# Revit family: Univers-IP44-leer-Unterputz-AT-de
name_source: partatom
category: Electrical Equipment
units: mm (PartAtom-declared; Revit-internal decimal feet)

## family parameters
Cut with Voids When Loaded = No
Host = Face
Panel Configuration = Two Columns, Circuits Across
Part Type = Panelboard
Room Calculation Point = No
Round Connector Dimension = Use Diameter
Shared = No

## types (21) — shared parameters
EF000003 - Montageart = EV001247 - Aufputz/Unterputz
EF000007 - Farbe = EV000202 - weiß
EF000116 - RAL-Nummer = 9010
EF000118 - Mit Montageplatte = No
EF000339 - Art der Abdeckung = EV004216 - Tür
EF001062 - EMV-Ausführung = No
EF001088 - Anbaumöglichkeit = No
EF001134 - DIN-Schiene = No
EF001596 - Werkstoff des Gehäuses = EV000179 - Stahl
EF005474 - Schutzart (IP) = EV006418 - IP44
EF006244 - Transparenter Deckel/Tür = No
EF006306 - Mit Schloss = No
EF015776 - Erdungsklemmenblock = No
EF015777 - Neutralleiterklemmenblock = No
EF015941 - Signaldurchlassende Tür = No
HG000002 - Mit tür = Yes
HG000003 - Bereich = Univers
HG000005 - Dicke = 3 mm  [stored 0.00984252 ft]
HG000006 - Unterputz = Yes
HG000011 - Leere Reihen von unten = No
Manufacturer = Hager
Type Comments = Univers
zero-valued in all types: Default Elevation, EF000266 - Anzahl der Reihen, EF002950 - Breite in Teilungseinheiten, HG000001 - Anzahl der Spalten, HG000007 - Anzahl der leeren Spalten, HG000008 - Anzahl der leeren Reihen

## per-type parameters (varying)
| type | EF000008 - Breite | EF000040 - Höhe | EF000049 - Tiefe | EF000218 - Einbautiefe | EF000332 - Einbauhöhe | EF000846 - Einbaubreite | EF001131 - Innentiefe | EF004462 - Art der Schließung | EF009212 - Ausführung Deckel | HG000004 - Herstellerreferenz | HG000009 - Doppelflügeligen Tür | HG000010 - Asymmetrische Türen | Model |
| Unterputz IP44 B1050 H1100 T161 0 Teilungseinheiten - FWB74D | 1050 mm | 1100 mm | 161 mm  [stored 0.528215 ft] | 161 mm  [stored 0.528215 ft] | 1100 mm | 1050 mm | 160 mm  [stored 0.524934 ft] | EV000154 - sonstige | EV000116 - geschlossen | FWB74D | Yes | No | FWB74D |
| Unterputz IP44 B1050 H500 T161 0 Teilungseinheiten - FWB34D | 1050 mm | 500 mm  [stored 1.64042 ft] | 161 mm  [stored 0.528215 ft] | 161 mm  [stored 0.528215 ft] | 500 mm  [stored 1.64042 ft] | 1050 mm | 156 mm  [stored 0.511811 ft] | EV000154 - sonstige | EV000116 - geschlossen | FWB34D | Yes | No | FWB34D |
| Unterputz IP44 B1050 H650 T161 0 Teilungseinheiten - FWB44D | 1050 mm | 650 mm  [stored 2.13255 ft] | 161 mm  [stored 0.528215 ft] | 161 mm  [stored 0.528215 ft] | 650 mm  [stored 2.13255 ft] | 1050 mm | 156 mm  [stored 0.511811 ft] | EV000154 - sonstige | EV000116 - geschlossen | FWB44D | Yes | No | FWB44D |
| Unterputz IP44 B1050 H800 T161 0 Teilungseinheiten - FWB54D | 1050 mm | 800 mm  [stored 2.62467 ft] | 161 mm  [stored 0.528215 ft] | 161 mm  [stored 0.528215 ft] | 800 mm  [stored 2.62467 ft] | 1050 mm | 156 mm  [stored 0.511811 ft] | EV000154 - sonstige | EV000116 - geschlossen | FWB54D | Yes | No | FWB54D |
| Unterputz IP44 B1050 H950 T161 0 Teilungseinheiten - FWB64D | 1050 mm | 950 mm  [stored 3.1168 ft] | 161 mm  [stored 0.528215 ft] | 161 mm  [stored 0.528215 ft] | 950 mm  [stored 3.1168 ft] | 1050 mm | 156 mm  [stored 0.511811 ft] | EV000154 - sonstige | EV000116 - geschlossen | FWB64D | Yes | No | FWB64D |
| Unterputz IP44 B300 H1100 T161 0 Teilungseinheiten - FWB71D | 300 mm | 1100 mm | 161 mm  [stored 0.528215 ft] | 161 mm  [stored 0.528215 ft] | 1100 mm | 300 mm | 160 mm  [stored 0.524934 ft] | EV000154 - sonstige | EV000116 - geschlossen | FWB71D | No | No | FWB71D |
| Unterputz IP44 B300 H1250 T160 0 Teilungseinheiten - FWB81D | 300 mm | 1250 mm  [stored 4.10105 ft] | 160 mm  [stored 0.524934 ft] | 160 mm  [stored 0.524934 ft] | 1250 mm  [stored 4.10105 ft] | 300 mm | 160 mm  [stored 0.524934 ft] | 0 | EV000116 - geschlossen | FWB81D | No | No | FWB81D |
| Unterputz IP44 B300 H500 T161 0 Teilungseinheiten - FWB31D | 300 mm | 500 mm  [stored 1.64042 ft] | 161 mm  [stored 0.528215 ft] | 161 mm  [stored 0.528215 ft] | 500 mm  [stored 1.64042 ft] | 300 mm | 156 mm  [stored 0.511811 ft] | EV000154 - sonstige | EV000116 - geschlossen | FWB31D | No | No | FWB31D |
| Unterputz IP44 B300 H650 T161 0 Teilungseinheiten - FWB41D | 300 mm | 650 mm  [stored 2.13255 ft] | 161 mm  [stored 0.528215 ft] | 161 mm  [stored 0.528215 ft] | 650 mm  [stored 2.13255 ft] | 300 mm | 160 mm  [stored 0.524934 ft] | EV000154 - sonstige | EV000116 - geschlossen | FWB41D | No | No | FWB41D |
| Unterputz IP44 B300 H800 T161 0 Teilungseinheiten - FWB51D | 300 mm | 800 mm  [stored 2.62467 ft] | 161 mm  [stored 0.528215 ft] | 161 mm  [stored 0.528215 ft] | 800 mm  [stored 2.62467 ft] | 300 mm | 160 mm  [stored 0.524934 ft] | EV000154 - sonstige | EV000116 - geschlossen | FWB51D | No | No | FWB51D |
| Unterputz IP44 B300 H950 T161 0 Teilungseinheiten - FWB61D | 300 mm | 950 mm  [stored 3.1168 ft] | 161 mm  [stored 0.528215 ft] | 161 mm  [stored 0.528215 ft] | 950 mm  [stored 3.1168 ft] | 300 mm | 160 mm  [stored 0.524934 ft] | EV000154 - sonstige | EV000116 - geschlossen | FWB61D | No | No | FWB61D |
| Unterputz IP44 B550 H1100 T161 0 Teilungseinheiten - FWB72D | 550 mm | 1100 mm | 161 mm  [stored 0.528215 ft] | 161 mm  [stored 0.528215 ft] | 1100 mm | 550 mm | 160 mm  [stored 0.524934 ft] | EV000154 - sonstige | EV000116 - geschlossen | FWB72D | No | No | FWB72D |
| Unterputz IP44 B550 H500 T161 0 Teilungseinheiten - FWB32D | 550 mm | 500 mm  [stored 1.64042 ft] | 161 mm  [stored 0.528215 ft] | 161 mm  [stored 0.528215 ft] | 500 mm  [stored 1.64042 ft] | 550 mm | 156 mm  [stored 0.511811 ft] | EV000154 - sonstige | EV000116 - geschlossen | FWB32D | No | No | FWB32D |
| Unterputz IP44 B550 H650 T161 0 Teilungseinheiten - FWB42D | 550 mm | 650 mm  [stored 2.13255 ft] | 161 mm  [stored 0.528215 ft] | 161 mm  [stored 0.528215 ft] | 650 mm  [stored 2.13255 ft] | 550 mm | 160 mm  [stored 0.524934 ft] | EV000154 - sonstige | EV000116 - geschlossen | FWB42D | No | No | FWB42D |
| Unterputz IP44 B550 H800 T161 0 Teilungseinheiten - FWB52D | 550 mm | 800 mm  [stored 2.62467 ft] | 161 mm  [stored 0.528215 ft] | 161 mm  [stored 0.528215 ft] | 800 mm  [stored 2.62467 ft] | 550 mm | 160 mm  [stored 0.524934 ft] | EV000154 - sonstige | EV000116 - geschlossen | FWB52D | No | No | FWB52D |
| Unterputz IP44 B550 H950 T161 0 Teilungseinheiten - FWB62D | 550 mm | 950 mm  [stored 3.1168 ft] | 161 mm  [stored 0.528215 ft] | 161 mm  [stored 0.528215 ft] | 950 mm  [stored 3.1168 ft] | 550 mm | 160 mm  [stored 0.524934 ft] | EV000154 - sonstige | EV000116 - geschlossen | FWB62D | No | No | FWB62D |
| Unterputz IP44 B800 H1100 T161 0 Teilungseinheiten - FWB73D | 800 mm  [stored 2.62467 ft] | 1100 mm | 161 mm  [stored 0.528215 ft] | 161 mm  [stored 0.528215 ft] | 1100 mm | 800 mm  [stored 2.62467 ft] | 156 mm  [stored 0.511811 ft] | EV000154 - sonstige | EV000116 - geschlossen | FWB73D | Yes | Yes | FWB73D |
| Unterputz IP44 B800 H500 T161 0 Teilungseinheiten - FWB33D | 800 mm  [stored 2.62467 ft] | 500 mm  [stored 1.64042 ft] | 161 mm  [stored 0.528215 ft] | 161 mm  [stored 0.528215 ft] | 500 mm  [stored 1.64042 ft] | 800 mm  [stored 2.62467 ft] | 160 mm  [stored 0.524934 ft] | EV000154 - sonstige | EV000116 - geschlossen | FWB33D | Yes | Yes | FWB33D |
| Unterputz IP44 B800 H650 T161 0 Teilungseinheiten - FWB43D | 800 mm  [stored 2.62467 ft] | 650 mm  [stored 2.13255 ft] | 161 mm  [stored 0.528215 ft] | 161 mm  [stored 0.528215 ft] | 650 mm  [stored 2.13255 ft] | 800 mm  [stored 2.62467 ft] | 160 mm  [stored 0.524934 ft] | EV000154 - sonstige | EV009916 - mit Ausschnitt | FWB43D | Yes | Yes | FWB43D |
| Unterputz IP44 B800 H800 T161 0 Teilungseinheiten - FWB53D | 800 mm  [stored 2.62467 ft] | 800 mm  [stored 2.62467 ft] | 161 mm  [stored 0.528215 ft] | 161 mm  [stored 0.528215 ft] | 800 mm  [stored 2.62467 ft] | 800 mm  [stored 2.62467 ft] | 160 mm  [stored 0.524934 ft] | EV000154 - sonstige | EV000116 - geschlossen | FWB53D | Yes | Yes | FWB53D |
| Unterputz IP44 B800 H950 T161 0 Teilungseinheiten - FWB63D | 800 mm  [stored 2.62467 ft] | 950 mm  [stored 3.1168 ft] | 161 mm  [stored 0.528215 ft] | 161 mm  [stored 0.528215 ft] | 950 mm  [stored 3.1168 ft] | 800 mm  [stored 2.62467 ft] | 156 mm  [stored 0.511811 ft] | EV000154 - sonstige | EV000116 - geschlossen | FWB63D | Yes | Yes | FWB63D |

note: [stored X ft] marks values corroborated as IEEE doubles in the binary element streams (Revit-internal decimal feet)

## geometry (parser evidence)
native form markers: Sweep x12
no freeform markers — native parametric forms only
